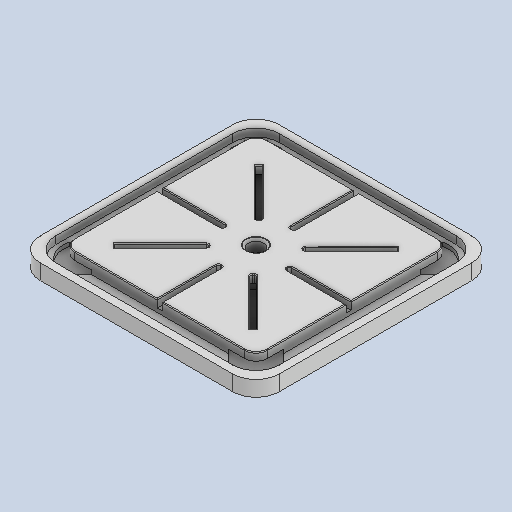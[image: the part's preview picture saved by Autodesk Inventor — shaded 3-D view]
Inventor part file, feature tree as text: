
AUTODESK INVENTOR PART (.ipt)
format: ipt  version: 2024.2 (Build 282272000, 272)  size: 246,272 bytes
history: native  units: in
note: dims shown in document units (in); Inventor stores cm internally (conversion verified against a paired STEP export)
features: fillet x1
ambient origin geometry x8: Origin, YZ Plane, XZ Plane, XY Plane, X Axis, Y Axis, Z Axis, Center Point
bodies: Solid1 (feature_tree)
feature tree (1):
  fillet  "Fillet1"  [1 undecoded]
note: 1 required parameter value undecoded (feature->parameter linkage not recoverable at this tier; creation-order binding heuristic only, values carry confidence <= 0.55)
